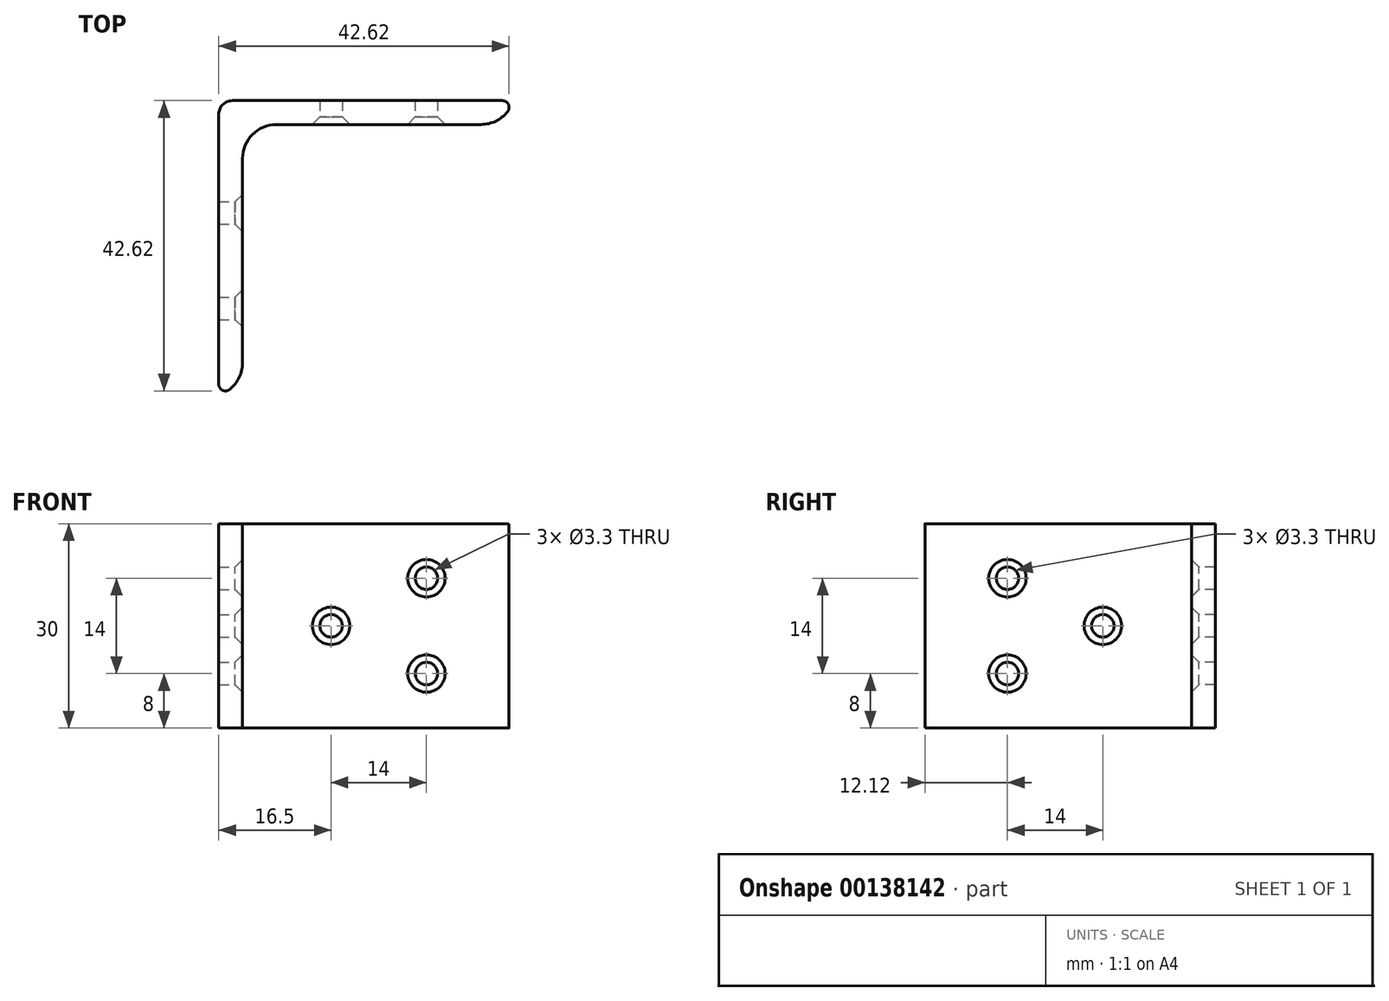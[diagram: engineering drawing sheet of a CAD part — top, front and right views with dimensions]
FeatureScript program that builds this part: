
annotation { "Feature Type Name" : "Feature", "Feature Type Description" : "" }
export const myFeature = defineFeature(function(context is Context, id is Id, definition is map)
    precondition{}
    {
        {
            var Q0;
            Q0=qCreatedBy(makeId("Top.planeOp"),FACE);
            var sketch = newSketch(context, id + "F0", { "sketchPlane" : qUnion([Q0])});
            skLineSegment(sketch, "E0", {"start": v(0, -35) * mm, "end": v(0, -5) * mm});
            skLineSegment(sketch, "E1", {"start": v(5, 0) * mm, "end": v(35, 0) * mm});
            skLineSegment(sketch, "E2", {"start": v(40, 3.5) * mm, "end": v(40, 5) * mm});
            skLineSegment(sketch, "E3", {"start": v(40, 3.5) * mm, "end": v(-1.5, 3.5) * mm});
            skLineSegment(sketch, "E4", {"start": v(-3.5, 1.5) * mm, "end": v(-3.5, -40) * mm});
            skLineSegment(sketch, "E5", {"start": v(-5, -40) * mm, "end": v(-3.5, -40) * mm});
            skPoint(sketch, "E6.visualSharp", {"position": v(0, 0) * mm});
            skArc(sketch, "E6.filletArc", {"start": v(5, 0) * mm, "mid": v(1.46, -1.46) * mm, "end": v(0, -5) * mm});
            skPoint(sketch, "E7.visualSharp", {"position": v(40, 0) * mm});
            skArc(sketch, "E7.filletArc", {"start": v(35, 0) * mm, "mid": v(38.54, 1.46) * mm, "end": v(40, 5) * mm});
            skPoint(sketch, "E8.visualSharp", {"position": v(0, -40) * mm});
            skArc(sketch, "E8.filletArc", {"start": v(-5, -40) * mm, "mid": v(-1.46, -38.54) * mm, "end": v(0, -35) * mm});
            skPoint(sketch, "E9.visualSharp", {"position": v(-3.5, 3.5) * mm});
            skArc(sketch, "E9.filletArc", {"start": v(-1.5, 3.5) * mm, "mid": v(-2.91, 2.91) * mm, "end": v(-3.5, 1.5) * mm});
            skSolve(sketch);
        }
        {
            var Q0;
            Q0=makeQuery(id+"F0.imprint","IMPRINT",FACE,{"disambiguationData":[TD([[makeQuery(id+"F0.imprint","IMPRINT",EDGE,{"derivedFrom":sQuery(id+"F0.wireOp",EDGE,"E0")}),1.0]])]});
            extrude(context, id + "F1", {"entities" : qUnion([Q0]), "depth" : 30 * mm});
        }
        {
            var Q0;
            Q0=makeQuery(id+"F1.opExtrude","SWEPT_FACE",FACE,{"disambiguationData":[OSD([sQuery(id+"F0.wireOp",EDGE,"E1")])]});
            var sketch = newSketch(context, id + "F2", { "sketchPlane" : qUnion([Q0])});
            skPoint(sketch, "E10", {"position": v(13, 15) * mm});
            skPoint(sketch, "E11", {"position": v(27, 22) * mm});
            skPoint(sketch, "E12", {"position": v(27, 8) * mm});
            skPoint(sketch, "E13", {"position": v(35, 15) * mm});
            skSolve(sketch);
        }
        {
            var Q0;
            Q0=makeQuery(id+"F1.opExtrude","SWEPT_FACE",FACE,{"disambiguationData":[OSD([sQuery(id+"F0.wireOp",EDGE,"E0")])]});
            var sketch = newSketch(context, id + "F3", { "sketchPlane" : qUnion([Q0])});
            skPoint(sketch, "E14", {"position": v(-35, 15) * mm});
            skPoint(sketch, "E15", {"position": v(-13, 15) * mm});
            skPoint(sketch, "E16", {"position": v(-27, 22) * mm});
            skPoint(sketch, "E17", {"position": v(-27, 8) * mm});
            skSolve(sketch);
        }
        {
            var Q0;
            Q0=sQuery(id+"F2.wireOp",VERTEX,"E10");
            var Q1;
            Q1=sQuery(id+"F2.wireOp",VERTEX,"E11");
            var Q2;
            Q2=sQuery(id+"F2.wireOp",VERTEX,"E12");
            var Q3;
            Q3=sQuery(id+"F3.wireOp",VERTEX,"E15");
            var Q4;
            Q4=sQuery(id+"F3.wireOp",VERTEX,"E16");
            var Q5;
            Q5=sQuery(id+"F3.wireOp",VERTEX,"E17");
            var Q6;
            Q6=makeQuery(id+"F1.opExtrude","SWEPT_BODY",BODY,{"disambiguationData":[OSD([sQuery(id+"F0.wireOp",EDGE,"E0"),sQuery(id+"F0.wireOp",EDGE,"E1"),sQuery(id+"F0.wireOp",EDGE,"E3"),sQuery(id+"F0.wireOp",EDGE,"E4"),sQuery(id+"F0.wireOp",EDGE,"E6.filletArc"),sQuery(id+"F0.wireOp",EDGE,"E7.filletArc"),sQuery(id+"F0.wireOp",EDGE,"E8.filletArc")])]});
            hole(context, id + "F4", {"style" : HoleStyle.C_SINK, "endStyle" : HoleEndStyle.THROUGH, "holeDiameter" : 3.3 * mm, "cSinkDiameter" : 5.5 * mm, "cSinkAngle" : 90 * degree, "locations" : qUnion([Q0, Q1, Q2, Q3, Q4, Q5]), "scope" : qUnion([Q6]), "isTappedThrough" : true});
        }
        {
            var Q0;
            Q0=makeQuery(id+"F1.opExtrude","SWEPT_EDGE",EDGE,{"disambiguationData":[OSD([sQuery(id+"F0.wireOp",EDGE,"E4"),sQuery(id+"F0.wireOp",EDGE,"E8.filletArc")])]});
            var Q1;
            Q1=makeQuery(id+"F1.opExtrude","SWEPT_EDGE",EDGE,{"disambiguationData":[OSD([sQuery(id+"F0.wireOp",EDGE,"E3"),sQuery(id+"F0.wireOp",EDGE,"E7.filletArc")])]});
            fillet(context, id + "F5", {"entities" : qUnion([Q0, Q1]), "radius" : 1 * mm, "tangentPropagation" : true, "allowEdgeOverflow" : false});
        }
    });
